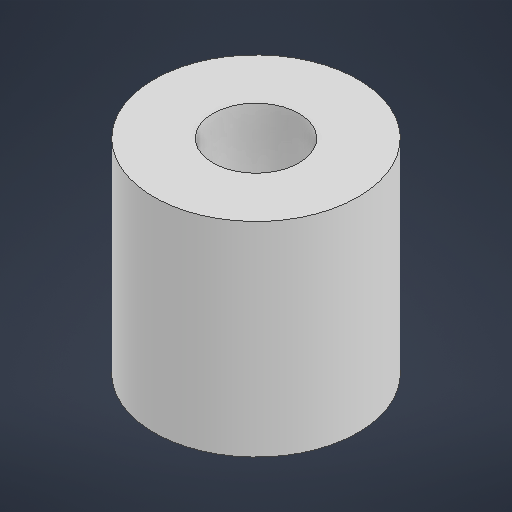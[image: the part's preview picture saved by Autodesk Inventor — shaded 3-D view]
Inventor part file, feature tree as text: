
AUTODESK INVENTOR PART (.ipt)
format: ipt  version: 2025.1 (Build 291241000, 241)  size: 178,176 bytes
history: native  units: mm
features: extrude x2, sketch x1
ambient origin geometry x8: Origin, YZ Plane, XZ Plane, XY Plane, X Axis, Y Axis, Z Axis, Center Point
bodies: Solid1 (feature_tree)
feature tree (3):
  sketch  "Sketch1"  dims[d0=19.0mm d1=5.0mm d2=8.0mm d3=19.0mm d4=0.0mm d5=9.5mm d6=0.0mm]
  extrude  "Extrusion1"  Depth=9.5mm
  extrude  "Extrusion2"  Depth=9.5mm
